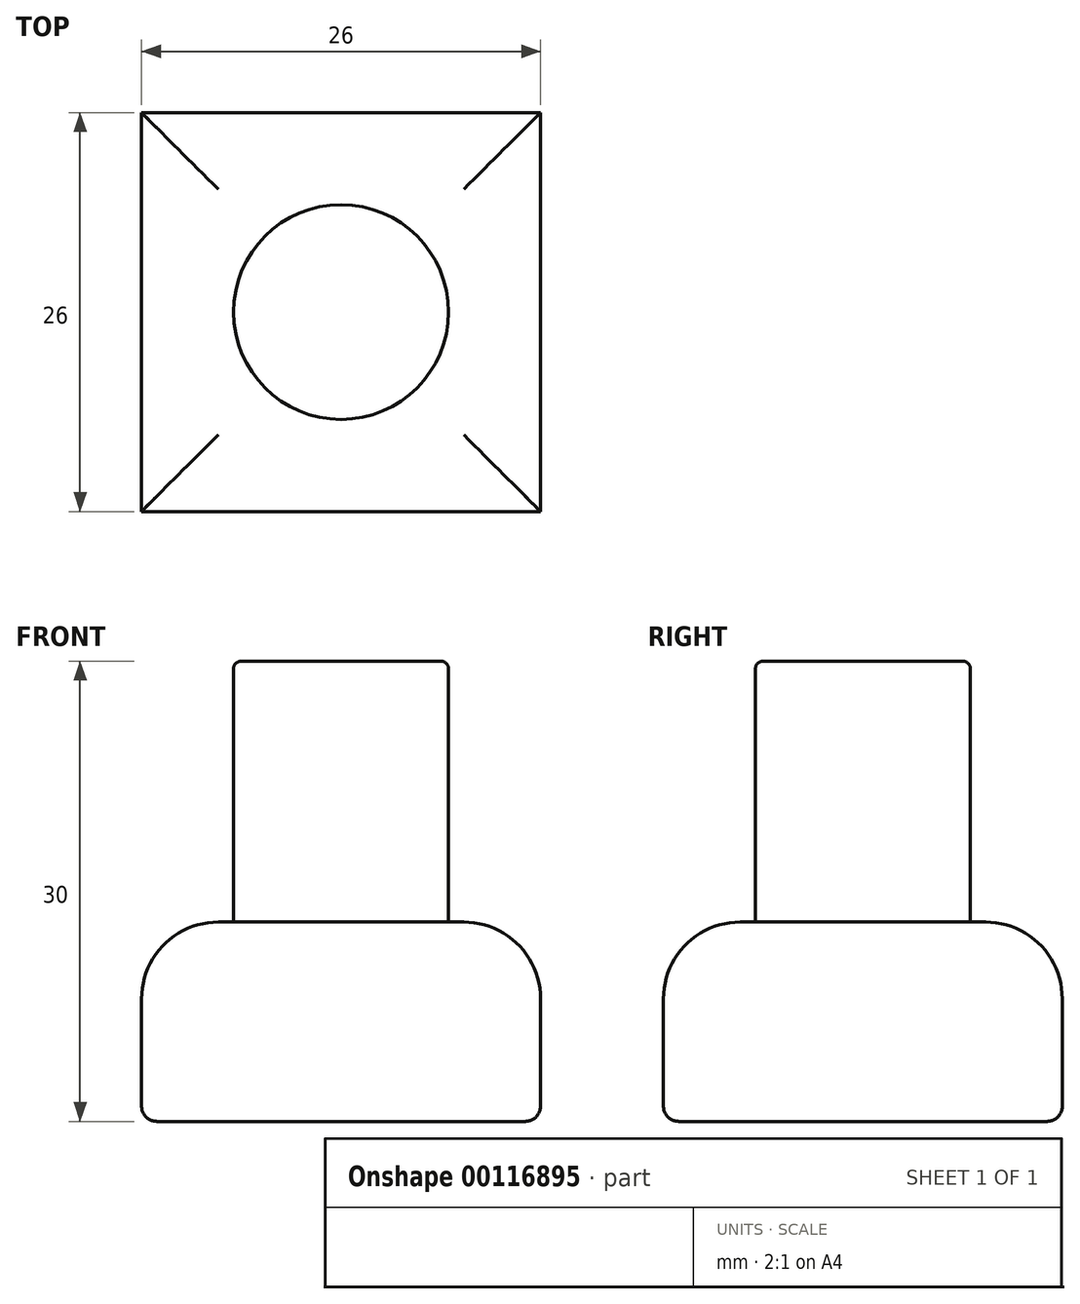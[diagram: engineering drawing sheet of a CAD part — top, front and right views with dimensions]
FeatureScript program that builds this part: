
annotation { "Feature Type Name" : "Feature", "Feature Type Description" : "" }
export const myFeature = defineFeature(function(context is Context, id is Id, definition is map)
    precondition{}
    {
        {
            var Q0;
            Q0=qCreatedBy(makeId("Top.planeOp"),FACE);
            var sketch = newSketch(context, id + "F0", { "sketchPlane" : qUnion([Q0])});
            skLineSegment(sketch, "E0.bottom", {"start": v(-54.66, 39.97) * mm, "end": v(-28.66, 39.97) * mm});
            skLineSegment(sketch, "E0.top", {"start": v(-54.66, 13.97) * mm, "end": v(-28.66, 13.97) * mm});
            skLineSegment(sketch, "E0.left", {"start": v(-54.66, 39.97) * mm, "end": v(-54.66, 13.97) * mm});
            skLineSegment(sketch, "E0.right", {"start": v(-28.66, 39.97) * mm, "end": v(-28.66, 13.97) * mm});
            skSolve(sketch);
        }
        {
            var Q0;
            Q0 = qSketchRegion(id + "F0", true);
            extrude(context, id + "F1", {"entities" : qUnion([Q0]), "depth" : 13 * mm});
        }
        {
            var Q0;
            Q0=makeQuery(id+"F1.opExtrude","CAP_EDGE",EDGE,{"disambiguationData":[OSD([sQuery(id+"F0.wireOp",EDGE,"E0.right")])],"isStart":true});
            var Q1;
            Q1=makeQuery(id+"F1.opExtrude","CAP_EDGE",EDGE,{"disambiguationData":[OSD([sQuery(id+"F0.wireOp",EDGE,"E0.bottom")])],"isStart":true});
            var Q2;
            Q2=makeQuery(id+"F1.opExtrude","CAP_EDGE",EDGE,{"disambiguationData":[OSD([sQuery(id+"F0.wireOp",EDGE,"E0.left")])],"isStart":true});
            var Q3;
            Q3=makeQuery(id+"F1.opExtrude","CAP_EDGE",EDGE,{"disambiguationData":[OSD([sQuery(id+"F0.wireOp",EDGE,"E0.top")])],"isStart":true});
            fillet(context, id + "F2", {"entities" : qUnion([Q0, Q1, Q2, Q3]), "radius" : 1 * mm, "tangentPropagation" : true, "allowEdgeOverflow" : false});
        }
        {
            var Q0;
            Q0=makeQuery(id+"F1.opExtrude","CAP_EDGE",EDGE,{"disambiguationData":[OSD([sQuery(id+"F0.wireOp",EDGE,"E0.bottom")])],"isStart":false});
            var Q1;
            Q1=makeQuery(id+"F1.opExtrude","CAP_EDGE",EDGE,{"disambiguationData":[OSD([sQuery(id+"F0.wireOp",EDGE,"E0.left")])],"isStart":false});
            var Q2;
            Q2=makeQuery(id+"F1.opExtrude","CAP_EDGE",EDGE,{"disambiguationData":[OSD([sQuery(id+"F0.wireOp",EDGE,"E0.top")])],"isStart":false});
            var Q3;
            Q3=makeQuery(id+"F1.opExtrude","CAP_EDGE",EDGE,{"disambiguationData":[OSD([sQuery(id+"F0.wireOp",EDGE,"E0.right")])],"isStart":false});
            fillet(context, id + "F3", {"entities" : qUnion([Q0, Q1, Q2, Q3]), "radius" : 5 * mm, "tangentPropagation" : true, "allowEdgeOverflow" : false});
        }
        {
            var Q0;
            Q0=makeQuery(id+"F1.opExtrude","CAP_FACE",FACE,{"disambiguationData":[OSD([sQuery(id+"F0.wireOp",EDGE,"E0.bottom"),sQuery(id+"F0.wireOp",EDGE,"E0.top"),sQuery(id+"F0.wireOp",EDGE,"E0.left"),sQuery(id+"F0.wireOp",EDGE,"E0.right")])],"isStart":false});
            var sketch = newSketch(context, id + "F4", { "sketchPlane" : qUnion([Q0])});
            skPoint(sketch, "E1", {"position": v(-41.66, 26.97) * mm});
            skPoint(sketch, "E1.positionSnap0", {"position": v(-49.66, 26.97) * mm});
            skPoint(sketch, "E1.positionSnap1", {"position": v(-41.66, 34.97) * mm});
            skCircle(sketch, "E2", {"center": v(-41.66, 26.97) * mm, "radius": 7 * mm});
            skSolve(sketch);
        }
        {
            var Q0;
            Q0 = qSketchRegion(id + "F4", true);
            extrude(context, id + "F5", {"entities" : qUnion([Q0]), "operationType" : NewBodyOperationType.ADD, "depth" : 17 * mm});
        }
        {
            var Q0;
            Q0=makeQuery(id+"F5.opExtrude","CAP_EDGE",EDGE,{"disambiguationData":[OSD([sQuery(id+"F4.wireOp",EDGE,"E2")])],"isStart":false});
            fillet(context, id + "F6", {"entities" : qUnion([Q0]), "radius" : 0.5 * mm, "tangentPropagation" : true, "allowEdgeOverflow" : false});
        }
    });
